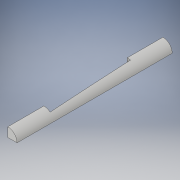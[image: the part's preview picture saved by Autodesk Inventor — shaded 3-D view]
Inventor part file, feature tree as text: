
AUTODESK INVENTOR PART (.ipt)
format: ipt  version: 2019.1 (Build 231200000, 200)  size: 122,880 bytes
history: native  units: in
note: dims shown in document units (in); Inventor stores cm internally (conversion verified against a paired STEP export)
features: extrude x3, sketch x2
ambient origin geometry x8: Origin, YZ Plane, XZ Plane, XY Plane, X Axis, Y Axis, Z Axis, Center Point
bodies: Solid1 (feature_tree)
feature tree (5):
  extrude  "Extrusion1"  Depth=6.375in TaperAngle=0.0deg
  extrude  "Extrusion2"  TaperAngle=0.0deg  [1 undecoded]
  extrude  "Extrusion3"  Depth=0.125in
  sketch  "Sketch1"  dims[d0=0.75in d1=6.375in d2=0.0in]
  sketch  "Sketch3"  dims[d4=1.5in d6=0.0in d7=0.0in d8=0.125in d9=0.25in d10=0.058in d11=0.036in d12=1.0in d13=0.0in]
note: 1 required parameter value undecoded (feature->parameter linkage not recoverable at this tier; creation-order binding heuristic only, values carry confidence <= 0.55)
